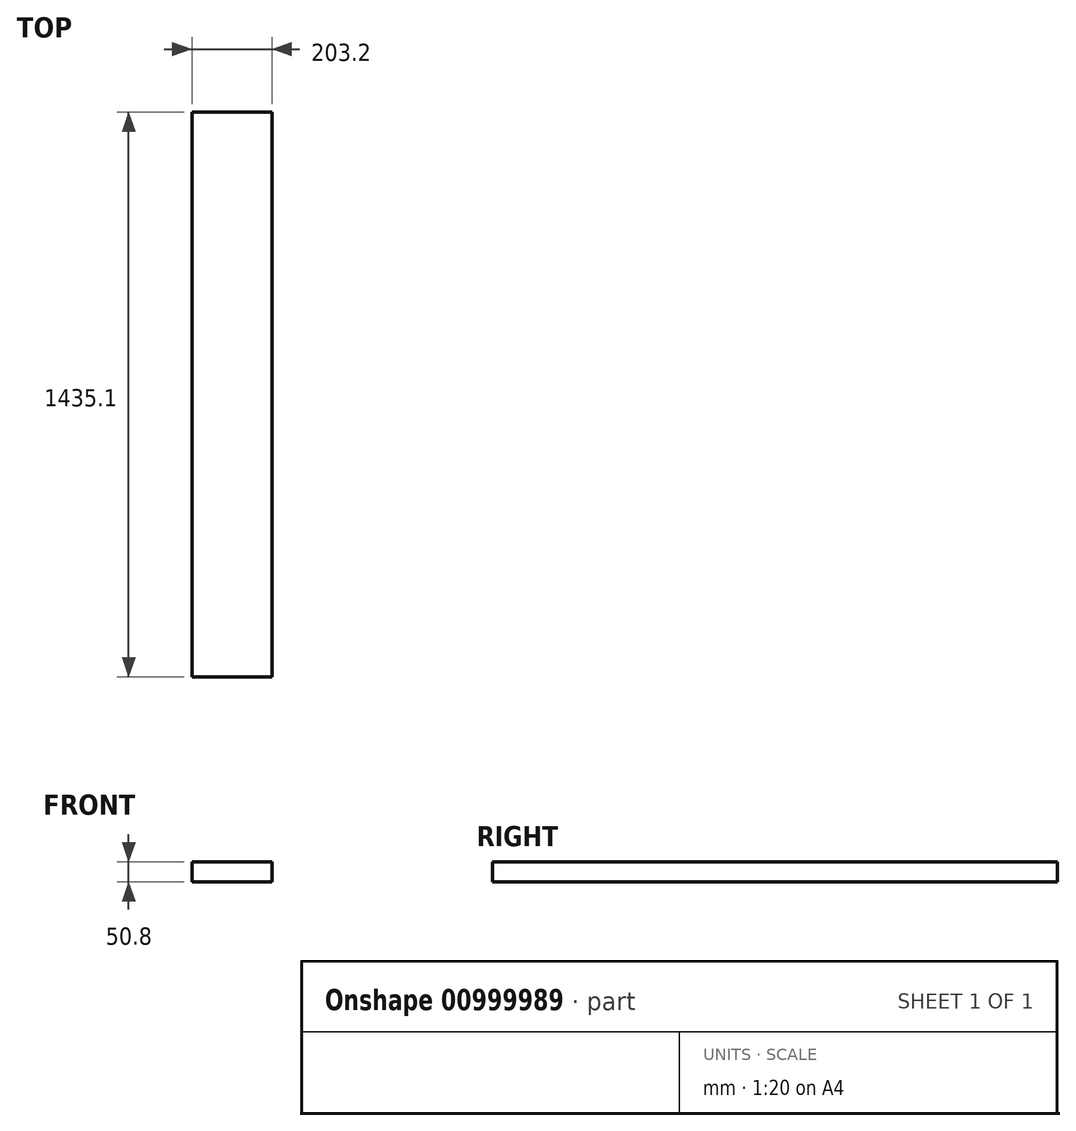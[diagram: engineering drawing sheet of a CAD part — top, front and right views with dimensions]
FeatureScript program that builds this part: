
annotation { "Feature Type Name" : "Feature", "Feature Type Description" : "" }
export const myFeature = defineFeature(function(context is Context, id is Id, definition is map)
    precondition{}
    {
        {
            var Q0;
            Q0=qCreatedBy(makeId("Front.planeOp"),FACE);
            var sketch = newSketch(context, id + "F0", { "sketchPlane" : qUnion([Q0])});
            skLineSegment(sketch, "E0.bottom", {"start": v(101.6, 25.4) * mm, "end": v(-101.6, 25.4) * mm});
            skLineSegment(sketch, "E0.top", {"start": v(101.6, -25.4) * mm, "end": v(-101.6, -25.4) * mm});
            skLineSegment(sketch, "E0.left", {"start": v(101.6, 25.4) * mm, "end": v(101.6, -25.4) * mm});
            skLineSegment(sketch, "E0.right", {"start": v(-101.6, 25.4) * mm, "end": v(-101.6, -25.4) * mm});
            skPoint(sketch, "E0.middle", {"position": v(0, 0) * mm});
            skSolve(sketch);
        }
        {
            var Q0;
            Q0=makeQuery(id+"F0.imprint","IMPRINT",FACE,{"disambiguationData":[TD([[makeQuery(id+"F0.imprint","IMPRINT",EDGE,{"derivedFrom":sQuery(id+"F0.wireOp",EDGE,"E0.bottom")}),1.0]])]});
            extrude(context, id + "F1", {"entities" : qUnion([Q0]), "depth" : 1435.1 * mm, "offsetDistance" : 25.4 * mm});
        }
    });
